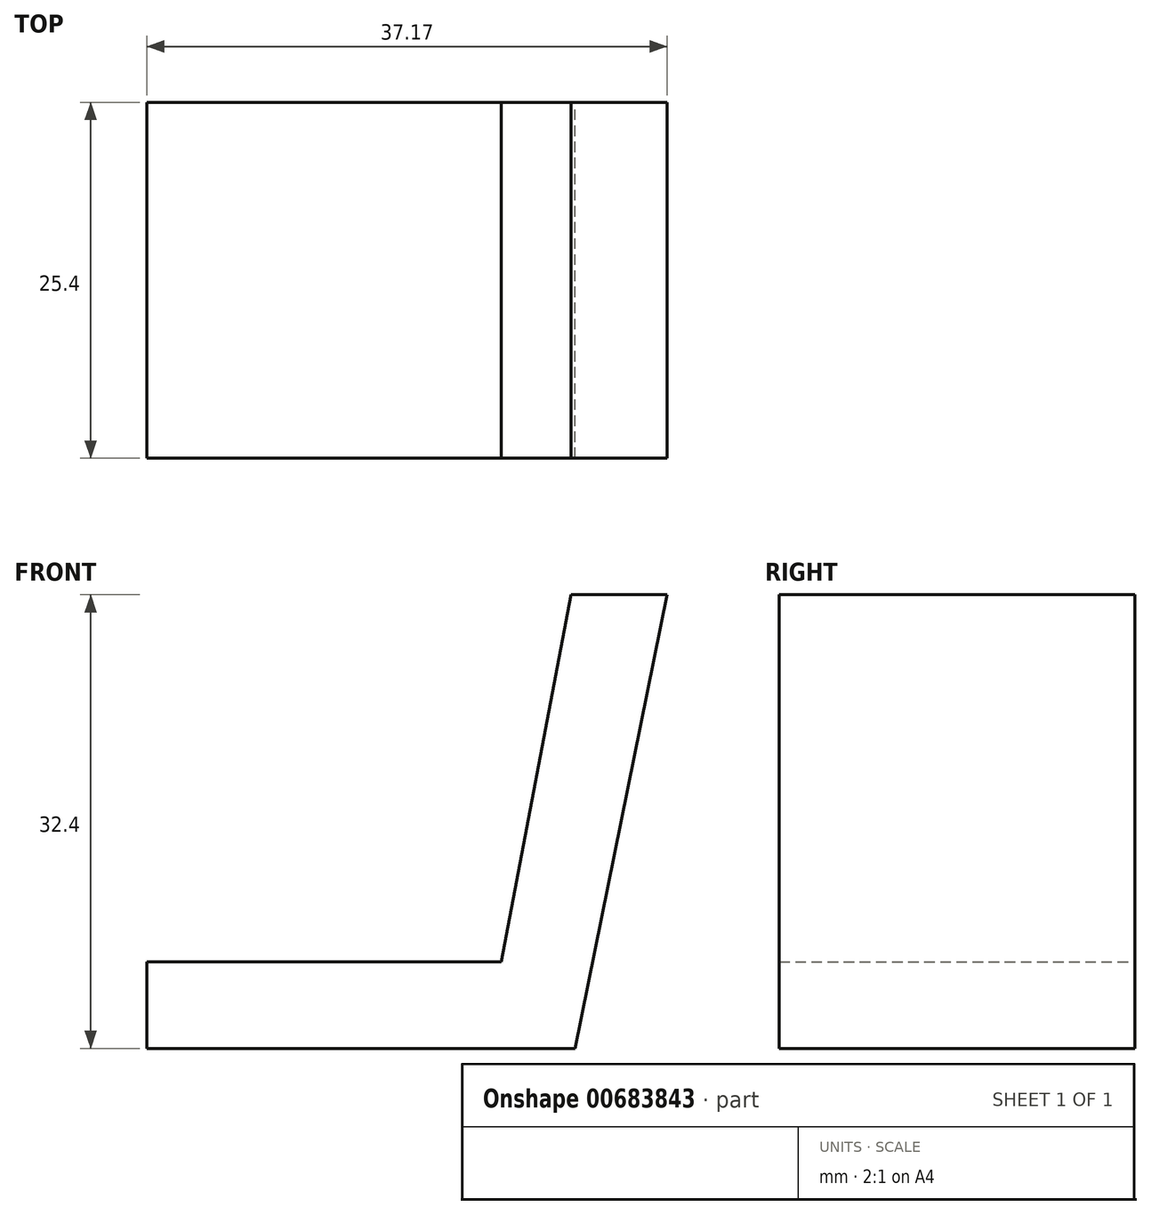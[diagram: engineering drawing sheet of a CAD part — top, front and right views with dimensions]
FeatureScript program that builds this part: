
annotation { "Feature Type Name" : "Feature", "Feature Type Description" : "" }
export const myFeature = defineFeature(function(context is Context, id is Id, definition is map)
    precondition{}
    {
        {
            var Q0;
            Q0=qCreatedBy(makeId("Front.planeOp"),FACE);
            var sketch = newSketch(context, id + "F0", { "sketchPlane" : qUnion([Q0])});
            skLineSegment(sketch, "E0.bottom", {"start": v(13.73, -4.75) * mm, "end": v(-16.84, -4.75) * mm});
            skLineSegment(sketch, "E0.right", {"start": v(-16.84, -4.75) * mm, "end": v(-16.84, 4.75) * mm});
            skPoint(sketch, "E0.middle", {"position": v(0, 0) * mm});
            skLineSegment(sketch, "E1", {"start": v(16.79, 33.66) * mm, "end": v(16.84, 33.82) * mm});
            skLineSegment(sketch, "E2", {"start": v(21.59, 33.82) * mm, "end": v(16.84, 33.82) * mm});
            skPoint(sketch, "E3.orphan", {"position": v(16.84, -4.75) * mm});
            skLineSegment(sketch, "E4", {"start": v(13.73, -4.75) * mm, "end": v(21.59, 33.82) * mm});
            skLineSegment(sketch, "E5", {"start": v(21.59, 33.82) * mm, "end": v(12.8, 33.53) * mm});
            skPoint(sketch, "E6.end.orphan", {"position": v(26.33, 33.82) * mm});
            skPoint(sketch, "E6.start.orphan", {"position": v(16.84, 4.75) * mm});
            skLineSegment(sketch, "E7", {"start": v(-16.84, 1.43) * mm, "end": v(8.47, 1.43) * mm});
            skLineSegment(sketch, "E8", {"start": v(8.47, 1.43) * mm, "end": v(13.45, 27.65) * mm});
            skLineSegment(sketch, "E9", {"start": v(13.45, 27.65) * mm, "end": v(20.33, 27.65) * mm});
            skSolve(sketch);
        }
        {
            var Q0;
            {var subQ0=sQuery(id+"F0.wireOp",EDGE,"E0.bottom");Q0=makeQuery(id+"F0.imprint","IMPRINT",FACE,{"disambiguationData":[TD([[makeQuery(id+"F0.imprint","IMPRINT",EDGE,{"derivedFrom":subQ0}),-1.0]])]});}
            extrude(context, id + "F1", {"entities" : qUnion([Q0]), "depth" : 12.7 * mm, "offsetDistance" : 25.4 * mm, "hasSecondDirection" : true, "secondDirectionOppositeDirection" : true, "secondDirectionDepth" : 12.7 * mm});
        }
    });
